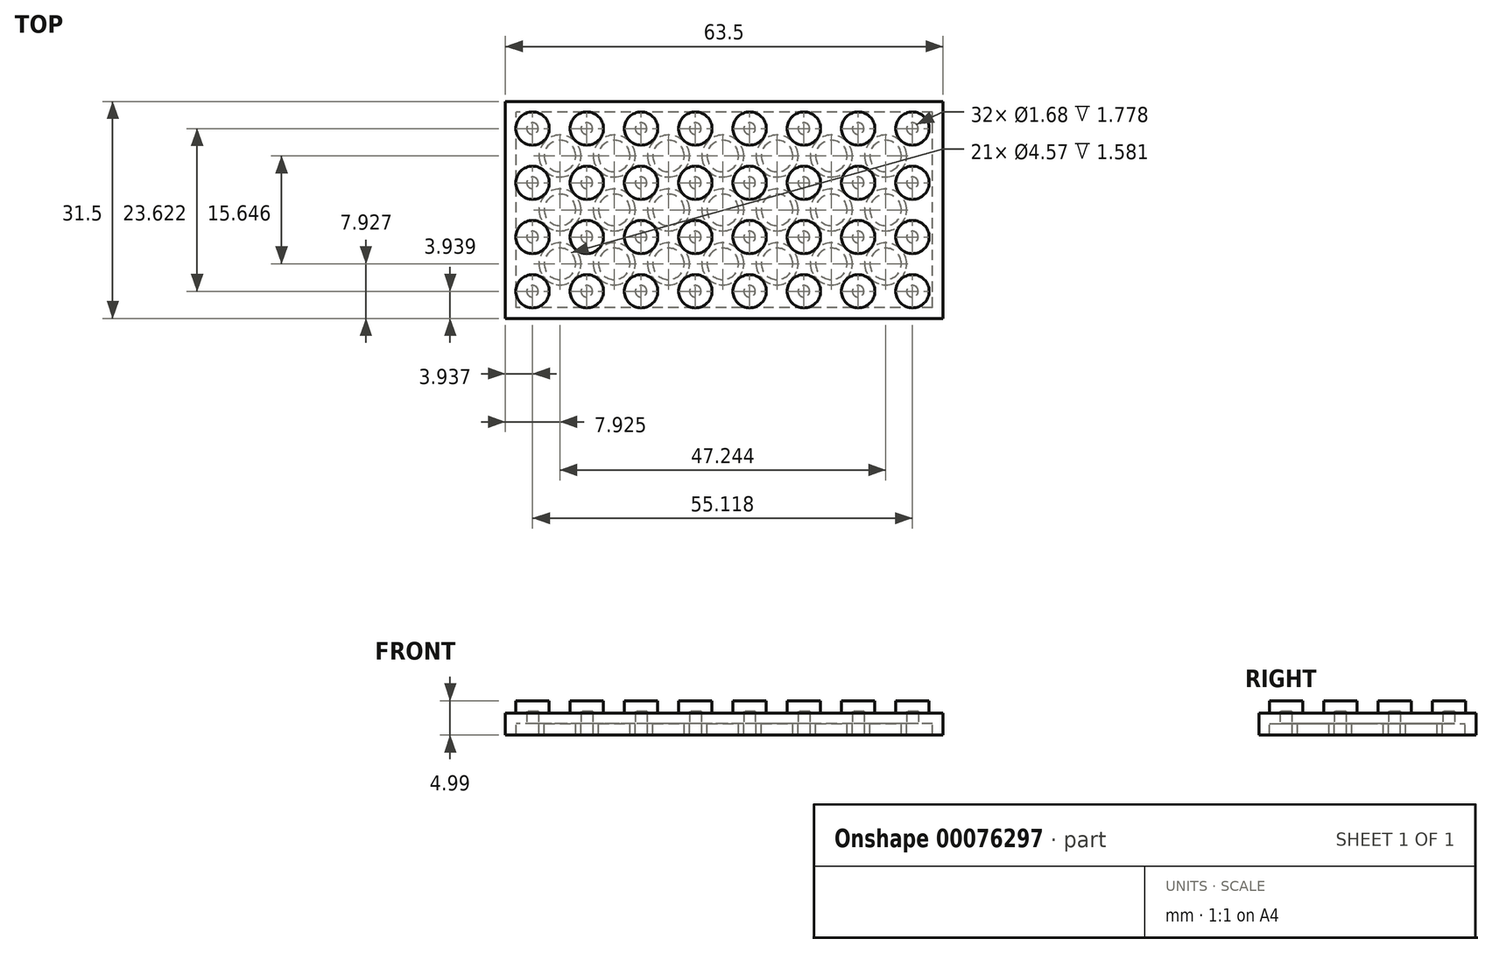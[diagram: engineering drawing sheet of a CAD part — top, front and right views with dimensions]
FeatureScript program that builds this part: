
annotation { "Feature Type Name" : "Feature", "Feature Type Description" : "" }
export const myFeature = defineFeature(function(context is Context, id is Id, definition is map)
    precondition{}
    {
        {
            var Q0;
            Q0=qCreatedBy(makeId("Top.planeOp"),FACE);
            var sketch = newSketch(context, id + "F0", { "sketchPlane" : qUnion([Q0])});
            skLineSegment(sketch, "E0.bottom", {"start": v(31.75, -15.75) * mm, "end": v(-31.75, -15.75) * mm});
            skLineSegment(sketch, "E0.top", {"start": v(31.75, 15.75) * mm, "end": v(-31.75, 15.75) * mm});
            skLineSegment(sketch, "E0.left", {"start": v(31.75, -15.75) * mm, "end": v(31.75, 15.75) * mm});
            skLineSegment(sketch, "E0.right", {"start": v(-31.75, -15.75) * mm, "end": v(-31.75, 15.75) * mm});
            skPoint(sketch, "E0.middle", {"position": v(0, 0) * mm});
            skSolve(sketch);
        }
        {
            var Q0;
            Q0=makeQuery(id+"F0.imprint","IMPRINT",FACE,{"disambiguationData":[TD([[makeQuery(id+"F0.imprint","IMPRINT",EDGE,{"derivedFrom":sQuery(id+"F0.wireOp",EDGE,"E0.bottom")}),-1.0]])]});
            extrude(context, id + "F1", {"entities" : qUnion([Q0]), "oppositeDirection" : true, "depth" : 3.2 * mm});
        }
        {
            var Q0;
            Q0=makeQuery(id+"F1.opExtrude","CAP_FACE",FACE,{"disambiguationData":[OSD([sQuery(id+"F0.wireOp",EDGE,"E0.bottom"),sQuery(id+"F0.wireOp",EDGE,"E0.top"),sQuery(id+"F0.wireOp",EDGE,"E0.left"),sQuery(id+"F0.wireOp",EDGE,"E0.right")])],"isStart":true});
            var sketch = newSketch(context, id + "F2", { "sketchPlane" : qUnion([Q0])});
            skCircle(sketch, "E1", {"center": v(-27.81, 11.81) * mm, "radius": 2.41 * mm});
            skCircle(sketch, "E2", {"center": v(-27.81, 3.94) * mm, "radius": 2.41 * mm});
            skCircle(sketch, "E3", {"center": v(-27.81, -3.94) * mm, "radius": 2.41 * mm});
            skCircle(sketch, "E4", {"center": v(-27.81, -11.81) * mm, "radius": 2.41 * mm});
            skCircle(sketch, "E5.1.0.0", {"center": v(-19.94, 11.81) * mm, "radius": 2.41 * mm});
            skCircle(sketch, "E5.1.0.1", {"center": v(-19.94, 3.94) * mm, "radius": 2.41 * mm});
            skCircle(sketch, "E5.1.0.2", {"center": v(-19.94, -3.94) * mm, "radius": 2.41 * mm});
            skCircle(sketch, "E5.1.0.3", {"center": v(-19.94, -11.81) * mm, "radius": 2.41 * mm});
            skCircle(sketch, "E5.2.0.0", {"center": v(-12.07, 11.81) * mm, "radius": 2.41 * mm});
            skCircle(sketch, "E5.2.0.1", {"center": v(-12.07, 3.94) * mm, "radius": 2.41 * mm});
            skCircle(sketch, "E5.2.0.2", {"center": v(-12.07, -3.94) * mm, "radius": 2.41 * mm});
            skCircle(sketch, "E5.2.0.3", {"center": v(-12.07, -11.81) * mm, "radius": 2.41 * mm});
            skCircle(sketch, "E5.3.0.0", {"center": v(-4.2, 11.81) * mm, "radius": 2.41 * mm});
            skCircle(sketch, "E5.3.0.1", {"center": v(-4.2, 3.94) * mm, "radius": 2.41 * mm});
            skCircle(sketch, "E5.3.0.2", {"center": v(-4.2, -3.94) * mm, "radius": 2.41 * mm});
            skCircle(sketch, "E5.3.0.3", {"center": v(-4.2, -11.81) * mm, "radius": 2.41 * mm});
            skCircle(sketch, "E5.4.0.0", {"center": v(3.68, 11.81) * mm, "radius": 2.41 * mm});
            skCircle(sketch, "E5.4.0.1", {"center": v(3.68, 3.94) * mm, "radius": 2.41 * mm});
            skCircle(sketch, "E5.4.0.2", {"center": v(3.68, -3.94) * mm, "radius": 2.41 * mm});
            skCircle(sketch, "E5.4.0.3", {"center": v(3.68, -11.81) * mm, "radius": 2.41 * mm});
            skCircle(sketch, "E5.5.0.0", {"center": v(11.56, 11.81) * mm, "radius": 2.41 * mm});
            skCircle(sketch, "E5.5.0.1", {"center": v(11.56, 3.94) * mm, "radius": 2.41 * mm});
            skCircle(sketch, "E5.5.0.2", {"center": v(11.56, -3.94) * mm, "radius": 2.41 * mm});
            skCircle(sketch, "E5.5.0.3", {"center": v(11.56, -11.81) * mm, "radius": 2.41 * mm});
            skCircle(sketch, "E5.6.0.0", {"center": v(19.43, 11.81) * mm, "radius": 2.41 * mm});
            skCircle(sketch, "E5.6.0.1", {"center": v(19.43, 3.94) * mm, "radius": 2.41 * mm});
            skCircle(sketch, "E5.6.0.2", {"center": v(19.43, -3.94) * mm, "radius": 2.41 * mm});
            skCircle(sketch, "E5.6.0.3", {"center": v(19.43, -11.81) * mm, "radius": 2.41 * mm});
            skCircle(sketch, "E5.7.0.0", {"center": v(27.3, 11.81) * mm, "radius": 2.41 * mm});
            skCircle(sketch, "E5.7.0.1", {"center": v(27.3, 3.94) * mm, "radius": 2.41 * mm});
            skCircle(sketch, "E5.7.0.2", {"center": v(27.3, -3.94) * mm, "radius": 2.41 * mm});
            skCircle(sketch, "E5.7.0.3", {"center": v(27.3, -11.81) * mm, "radius": 2.41 * mm});
            skLineSegment(sketch, "E5.direction1", {"start": v(-27.81, 11.81) * mm, "end": v(-19.94, 11.81) * mm, "construction": true});
            skSolve(sketch);
        }
        {
            var Q0;
            Q0=makeQuery(id+"F2.imprint","IMPRINT",FACE,{"disambiguationData":[TD([[makeQuery(id+"F2.imprint","IMPRINT",EDGE,{"derivedFrom":sQuery(id+"F2.wireOp",EDGE,"E1")}),1.0]])]});
            var Q1;
            Q1=makeQuery(id+"F2.imprint","IMPRINT",FACE,{"disambiguationData":[TD([[makeQuery(id+"F2.imprint","IMPRINT",EDGE,{"derivedFrom":sQuery(id+"F2.wireOp",EDGE,"E5.1.0.0")}),1.0]])]});
            var Q2;
            Q2=makeQuery(id+"F2.imprint","IMPRINT",FACE,{"disambiguationData":[TD([[makeQuery(id+"F2.imprint","IMPRINT",EDGE,{"derivedFrom":sQuery(id+"F2.wireOp",EDGE,"E5.2.0.0")}),1.0]])]});
            var Q3;
            Q3=makeQuery(id+"F2.imprint","IMPRINT",FACE,{"disambiguationData":[TD([[makeQuery(id+"F2.imprint","IMPRINT",EDGE,{"derivedFrom":sQuery(id+"F2.wireOp",EDGE,"E5.3.0.0")}),1.0]])]});
            var Q4;
            Q4=makeQuery(id+"F2.imprint","IMPRINT",FACE,{"disambiguationData":[TD([[makeQuery(id+"F2.imprint","IMPRINT",EDGE,{"derivedFrom":sQuery(id+"F2.wireOp",EDGE,"E5.4.0.0")}),1.0]])]});
            var Q5;
            Q5=makeQuery(id+"F2.imprint","IMPRINT",FACE,{"disambiguationData":[TD([[makeQuery(id+"F2.imprint","IMPRINT",EDGE,{"derivedFrom":sQuery(id+"F2.wireOp",EDGE,"E5.5.0.0")}),1.0]])]});
            var Q6;
            Q6=makeQuery(id+"F2.imprint","IMPRINT",FACE,{"disambiguationData":[TD([[makeQuery(id+"F2.imprint","IMPRINT",EDGE,{"derivedFrom":sQuery(id+"F2.wireOp",EDGE,"E5.6.0.0")}),1.0]])]});
            var Q7;
            Q7=makeQuery(id+"F2.imprint","IMPRINT",FACE,{"disambiguationData":[TD([[makeQuery(id+"F2.imprint","IMPRINT",EDGE,{"derivedFrom":sQuery(id+"F2.wireOp",EDGE,"E5.7.0.0")}),1.0]])]});
            var Q8;
            Q8=makeQuery(id+"F2.imprint","IMPRINT",FACE,{"disambiguationData":[TD([[makeQuery(id+"F2.imprint","IMPRINT",EDGE,{"derivedFrom":sQuery(id+"F2.wireOp",EDGE,"E5.7.0.1")}),1.0]])]});
            var Q9;
            Q9=makeQuery(id+"F2.imprint","IMPRINT",FACE,{"disambiguationData":[TD([[makeQuery(id+"F2.imprint","IMPRINT",EDGE,{"derivedFrom":sQuery(id+"F2.wireOp",EDGE,"E5.6.0.1")}),1.0]])]});
            var Q10;
            Q10=makeQuery(id+"F2.imprint","IMPRINT",FACE,{"disambiguationData":[TD([[makeQuery(id+"F2.imprint","IMPRINT",EDGE,{"derivedFrom":sQuery(id+"F2.wireOp",EDGE,"E5.5.0.1")}),1.0]])]});
            var Q11;
            Q11=makeQuery(id+"F2.imprint","IMPRINT",FACE,{"disambiguationData":[TD([[makeQuery(id+"F2.imprint","IMPRINT",EDGE,{"derivedFrom":sQuery(id+"F2.wireOp",EDGE,"E5.4.0.1")}),1.0]])]});
            var Q12;
            Q12=makeQuery(id+"F2.imprint","IMPRINT",FACE,{"disambiguationData":[TD([[makeQuery(id+"F2.imprint","IMPRINT",EDGE,{"derivedFrom":sQuery(id+"F2.wireOp",EDGE,"E5.3.0.1")}),1.0]])]});
            var Q13;
            Q13=makeQuery(id+"F2.imprint","IMPRINT",FACE,{"disambiguationData":[TD([[makeQuery(id+"F2.imprint","IMPRINT",EDGE,{"derivedFrom":sQuery(id+"F2.wireOp",EDGE,"E5.2.0.1")}),1.0]])]});
            var Q14;
            Q14=makeQuery(id+"F2.imprint","IMPRINT",FACE,{"disambiguationData":[TD([[makeQuery(id+"F2.imprint","IMPRINT",EDGE,{"derivedFrom":sQuery(id+"F2.wireOp",EDGE,"E5.1.0.1")}),1.0]])]});
            var Q15;
            Q15=makeQuery(id+"F2.imprint","IMPRINT",FACE,{"disambiguationData":[TD([[makeQuery(id+"F2.imprint","IMPRINT",EDGE,{"derivedFrom":sQuery(id+"F2.wireOp",EDGE,"E2")}),1.0]])]});
            var Q16;
            Q16=makeQuery(id+"F2.imprint","IMPRINT",FACE,{"disambiguationData":[TD([[makeQuery(id+"F2.imprint","IMPRINT",EDGE,{"derivedFrom":sQuery(id+"F2.wireOp",EDGE,"E3")}),1.0]])]});
            var Q17;
            Q17=makeQuery(id+"F2.imprint","IMPRINT",FACE,{"disambiguationData":[TD([[makeQuery(id+"F2.imprint","IMPRINT",EDGE,{"derivedFrom":sQuery(id+"F2.wireOp",EDGE,"E5.1.0.2")}),1.0]])]});
            var Q18;
            Q18=makeQuery(id+"F2.imprint","IMPRINT",FACE,{"disambiguationData":[TD([[makeQuery(id+"F2.imprint","IMPRINT",EDGE,{"derivedFrom":sQuery(id+"F2.wireOp",EDGE,"E5.2.0.2")}),1.0]])]});
            var Q19;
            Q19=makeQuery(id+"F2.imprint","IMPRINT",FACE,{"disambiguationData":[TD([[makeQuery(id+"F2.imprint","IMPRINT",EDGE,{"derivedFrom":sQuery(id+"F2.wireOp",EDGE,"E5.3.0.2")}),1.0]])]});
            var Q20;
            Q20=makeQuery(id+"F2.imprint","IMPRINT",FACE,{"disambiguationData":[TD([[makeQuery(id+"F2.imprint","IMPRINT",EDGE,{"derivedFrom":sQuery(id+"F2.wireOp",EDGE,"E5.4.0.2")}),1.0]])]});
            var Q21;
            Q21=makeQuery(id+"F2.imprint","IMPRINT",FACE,{"disambiguationData":[TD([[makeQuery(id+"F2.imprint","IMPRINT",EDGE,{"derivedFrom":sQuery(id+"F2.wireOp",EDGE,"E5.5.0.2")}),1.0]])]});
            var Q22;
            Q22=makeQuery(id+"F2.imprint","IMPRINT",FACE,{"disambiguationData":[TD([[makeQuery(id+"F2.imprint","IMPRINT",EDGE,{"derivedFrom":sQuery(id+"F2.wireOp",EDGE,"E5.6.0.2")}),1.0]])]});
            var Q23;
            Q23=makeQuery(id+"F2.imprint","IMPRINT",FACE,{"disambiguationData":[TD([[makeQuery(id+"F2.imprint","IMPRINT",EDGE,{"derivedFrom":sQuery(id+"F2.wireOp",EDGE,"E5.7.0.2")}),1.0]])]});
            var Q24;
            Q24=makeQuery(id+"F2.imprint","IMPRINT",FACE,{"disambiguationData":[TD([[makeQuery(id+"F2.imprint","IMPRINT",EDGE,{"derivedFrom":sQuery(id+"F2.wireOp",EDGE,"E5.7.0.3")}),1.0]])]});
            var Q25;
            Q25=makeQuery(id+"F2.imprint","IMPRINT",FACE,{"disambiguationData":[TD([[makeQuery(id+"F2.imprint","IMPRINT",EDGE,{"derivedFrom":sQuery(id+"F2.wireOp",EDGE,"E5.6.0.3")}),1.0]])]});
            var Q26;
            Q26=makeQuery(id+"F2.imprint","IMPRINT",FACE,{"disambiguationData":[TD([[makeQuery(id+"F2.imprint","IMPRINT",EDGE,{"derivedFrom":sQuery(id+"F2.wireOp",EDGE,"E5.5.0.3")}),1.0]])]});
            var Q27;
            Q27=makeQuery(id+"F2.imprint","IMPRINT",FACE,{"disambiguationData":[TD([[makeQuery(id+"F2.imprint","IMPRINT",EDGE,{"derivedFrom":sQuery(id+"F2.wireOp",EDGE,"E5.3.0.3")}),1.0]])]});
            var Q28;
            Q28=makeQuery(id+"F2.imprint","IMPRINT",FACE,{"disambiguationData":[TD([[makeQuery(id+"F2.imprint","IMPRINT",EDGE,{"derivedFrom":sQuery(id+"F2.wireOp",EDGE,"E5.2.0.3")}),1.0]])]});
            var Q29;
            Q29=makeQuery(id+"F2.imprint","IMPRINT",FACE,{"disambiguationData":[TD([[makeQuery(id+"F2.imprint","IMPRINT",EDGE,{"derivedFrom":sQuery(id+"F2.wireOp",EDGE,"E5.1.0.3")}),1.0]])]});
            var Q30;
            Q30=makeQuery(id+"F2.imprint","IMPRINT",FACE,{"disambiguationData":[TD([[makeQuery(id+"F2.imprint","IMPRINT",EDGE,{"derivedFrom":sQuery(id+"F2.wireOp",EDGE,"E4")}),1.0]])]});
            var Q31;
            Q31=makeQuery(id+"F2.imprint","IMPRINT",FACE,{"disambiguationData":[TD([[makeQuery(id+"F2.imprint","IMPRINT",EDGE,{"derivedFrom":sQuery(id+"F2.wireOp",EDGE,"E5.4.0.3")}),1.0]])]});
            extrude(context, id + "F3", {"entities" : qUnion([Q0, Q1, Q2, Q3, Q4, Q5, Q6, Q7, Q8, Q9, Q10, Q11, Q12, Q13, Q14, Q15, Q16, Q17, Q18, Q19, Q20, Q21, Q22, Q23, Q24, Q25, Q26, Q27, Q28, Q29, Q30, Q31]), "operationType" : NewBodyOperationType.ADD, "depth" : 1.78 * mm});
        }
        {
            var Q0;
            Q0=makeQuery(id+"F1.opExtrude","CAP_FACE",FACE,{"disambiguationData":[OSD([sQuery(id+"F0.wireOp",EDGE,"E0.bottom"),sQuery(id+"F0.wireOp",EDGE,"E0.top"),sQuery(id+"F0.wireOp",EDGE,"E0.left"),sQuery(id+"F0.wireOp",EDGE,"E0.right")])],"isStart":false});
            shell(context, id + "F4", {"entities" : qUnion([Q0]), "thickness" : 1.57 * mm});
        }
        {
            var Q0;
            Q0=makeQuery(id+"F4.opShell","OFFSET_FACE",FACE,{"disambiguationData":[OSD([sQuery(id+"F0.wireOp",EDGE,"E0.bottom"),sQuery(id+"F0.wireOp",EDGE,"E0.top"),sQuery(id+"F0.wireOp",EDGE,"E0.left"),sQuery(id+"F0.wireOp",EDGE,"E0.right")])]});
            var sketch = newSketch(context, id + "F5", { "sketchPlane" : qUnion([Q0])});
            skSolve(sketch);
        }
        {
            var Q0;
            {var subQ19=sQuery(id+"F0.wireOp",EDGE,"E0.bottom");Q0=makeQuery(id+"F5.imprint","IMPRINT",FACE,{"disambiguationData":[TD([[makeQuery(id+"F5.imprint","IMPRINT",EDGE,{"derivedFrom":makeQuery(id+"F4.opShell","OFFSET_EDGE",EDGE,{"disambiguationData":[OSD([subQ19]),TDD([makeQuery(id+"F1.opExtrude","CAP_EDGE",EDGE,{"disambiguationData":[OSD([subQ19])],"isStart":true})])]})}),1.0]])]});}
            var sketch = newSketch(context, id + "F6", { "sketchPlane" : qUnion([Q0])});
            skCircle(sketch, "E6", {"center": v(-23.83, 7.82) * mm, "radius": 3.05 * mm});
            skCircle(sketch, "E7", {"center": v(-23.83, 0) * mm, "radius": 3.05 * mm});
            skCircle(sketch, "E8", {"center": v(-23.83, -7.82) * mm, "radius": 3.05 * mm});
            skCircle(sketch, "E9.1.0.0", {"center": v(-15.95, 7.82) * mm, "radius": 3.05 * mm});
            skCircle(sketch, "E9.1.0.1", {"center": v(-15.95, 0) * mm, "radius": 3.05 * mm});
            skCircle(sketch, "E9.1.0.2", {"center": v(-15.95, -7.82) * mm, "radius": 3.05 * mm});
            skCircle(sketch, "E9.2.0.0", {"center": v(-8.08, 7.82) * mm, "radius": 3.05 * mm});
            skCircle(sketch, "E9.2.0.1", {"center": v(-8.08, 0) * mm, "radius": 3.05 * mm});
            skCircle(sketch, "E9.2.0.2", {"center": v(-8.08, -7.82) * mm, "radius": 3.05 * mm});
            skCircle(sketch, "E9.3.0.0", {"center": v(-0.2, 7.82) * mm, "radius": 3.05 * mm});
            skCircle(sketch, "E9.3.0.1", {"center": v(-0.2, 0) * mm, "radius": 3.05 * mm});
            skCircle(sketch, "E9.3.0.2", {"center": v(-0.2, -7.82) * mm, "radius": 3.05 * mm});
            skCircle(sketch, "E9.4.0.0", {"center": v(7.67, 7.82) * mm, "radius": 3.05 * mm});
            skCircle(sketch, "E9.4.0.1", {"center": v(7.67, 0) * mm, "radius": 3.05 * mm});
            skCircle(sketch, "E9.4.0.2", {"center": v(7.67, -7.82) * mm, "radius": 3.05 * mm});
            skCircle(sketch, "E9.5.0.0", {"center": v(15.54, 7.82) * mm, "radius": 3.05 * mm});
            skCircle(sketch, "E9.5.0.1", {"center": v(15.54, 0) * mm, "radius": 3.05 * mm});
            skCircle(sketch, "E9.5.0.2", {"center": v(15.54, -7.82) * mm, "radius": 3.05 * mm});
            skCircle(sketch, "E9.6.0.0", {"center": v(23.42, 7.82) * mm, "radius": 3.05 * mm});
            skCircle(sketch, "E9.6.0.1", {"center": v(23.42, 0) * mm, "radius": 3.05 * mm});
            skCircle(sketch, "E9.6.0.2", {"center": v(23.42, -7.82) * mm, "radius": 3.05 * mm});
            skCircle(sketch, "E10", {"center": v(-23.83, 7.82) * mm, "radius": 2.29 * mm});
            skCircle(sketch, "E11", {"center": v(-23.83, 0) * mm, "radius": 2.29 * mm});
            skCircle(sketch, "E12", {"center": v(-23.83, -7.82) * mm, "radius": 2.29 * mm});
            skCircle(sketch, "E13.1.0.0", {"center": v(-15.95, 7.82) * mm, "radius": 2.29 * mm});
            skCircle(sketch, "E13.1.0.1", {"center": v(-15.95, 0) * mm, "radius": 2.29 * mm});
            skCircle(sketch, "E13.1.0.2", {"center": v(-15.95, -7.82) * mm, "radius": 2.29 * mm});
            skCircle(sketch, "E13.2.0.0", {"center": v(-8.08, 7.82) * mm, "radius": 2.29 * mm});
            skCircle(sketch, "E13.2.0.1", {"center": v(-8.08, 0) * mm, "radius": 2.29 * mm});
            skCircle(sketch, "E13.2.0.2", {"center": v(-8.08, -7.82) * mm, "radius": 2.29 * mm});
            skCircle(sketch, "E13.3.0.0", {"center": v(-0.2, 7.82) * mm, "radius": 2.29 * mm});
            skCircle(sketch, "E13.3.0.1", {"center": v(-0.2, 0) * mm, "radius": 2.29 * mm});
            skCircle(sketch, "E13.3.0.2", {"center": v(-0.2, -7.82) * mm, "radius": 2.29 * mm});
            skCircle(sketch, "E13.4.0.0", {"center": v(7.67, 7.82) * mm, "radius": 2.29 * mm});
            skCircle(sketch, "E13.4.0.1", {"center": v(7.67, 0) * mm, "radius": 2.29 * mm});
            skCircle(sketch, "E13.4.0.2", {"center": v(7.67, -7.82) * mm, "radius": 2.29 * mm});
            skCircle(sketch, "E13.5.0.0", {"center": v(15.54, 7.82) * mm, "radius": 2.29 * mm});
            skCircle(sketch, "E13.5.0.1", {"center": v(15.54, 0) * mm, "radius": 2.29 * mm});
            skCircle(sketch, "E13.5.0.2", {"center": v(15.54, -7.82) * mm, "radius": 2.29 * mm});
            skCircle(sketch, "E13.6.0.0", {"center": v(23.42, 7.82) * mm, "radius": 2.29 * mm});
            skCircle(sketch, "E13.6.0.1", {"center": v(23.42, 0) * mm, "radius": 2.29 * mm});
            skCircle(sketch, "E13.6.0.2", {"center": v(23.42, -7.82) * mm, "radius": 2.29 * mm});
            skSolve(sketch);
        }
        {
            var Q0;
            Q0=makeQuery(id+"F6.imprint","IMPRINT",FACE,{"disambiguationData":[TD([[makeQuery(id+"F6.imprint","IMPRINT",EDGE,{"derivedFrom":sQuery(id+"F6.wireOp",EDGE,"E9.3.0.1")}),1.0]])]});
            var Q1;
            Q1=makeQuery(id+"F6.imprint","IMPRINT",FACE,{"disambiguationData":[TD([[makeQuery(id+"F6.imprint","IMPRINT",EDGE,{"derivedFrom":sQuery(id+"F6.wireOp",EDGE,"E9.6.0.1")}),1.0]])]});
            var Q2;
            Q2=makeQuery(id+"F6.imprint","IMPRINT",FACE,{"disambiguationData":[TD([[makeQuery(id+"F6.imprint","IMPRINT",EDGE,{"derivedFrom":sQuery(id+"F6.wireOp",EDGE,"E9.6.0.2")}),1.0]])]});
            var Q3;
            Q3=makeQuery(id+"F6.imprint","IMPRINT",FACE,{"disambiguationData":[TD([[makeQuery(id+"F6.imprint","IMPRINT",EDGE,{"derivedFrom":sQuery(id+"F6.wireOp",EDGE,"E9.5.0.2")}),1.0]])]});
            var Q4;
            Q4=makeQuery(id+"F6.imprint","IMPRINT",FACE,{"disambiguationData":[TD([[makeQuery(id+"F6.imprint","IMPRINT",EDGE,{"derivedFrom":sQuery(id+"F6.wireOp",EDGE,"E9.6.0.0")}),1.0]])]});
            var Q5;
            Q5=makeQuery(id+"F6.imprint","IMPRINT",FACE,{"disambiguationData":[TD([[makeQuery(id+"F6.imprint","IMPRINT",EDGE,{"derivedFrom":sQuery(id+"F6.wireOp",EDGE,"E9.5.0.1")}),1.0]])]});
            var Q6;
            Q6=makeQuery(id+"F6.imprint","IMPRINT",FACE,{"disambiguationData":[TD([[makeQuery(id+"F6.imprint","IMPRINT",EDGE,{"derivedFrom":sQuery(id+"F6.wireOp",EDGE,"E9.5.0.0")}),1.0]])]});
            var Q7;
            Q7=makeQuery(id+"F6.imprint","IMPRINT",FACE,{"disambiguationData":[TD([[makeQuery(id+"F6.imprint","IMPRINT",EDGE,{"derivedFrom":sQuery(id+"F6.wireOp",EDGE,"E9.4.0.1")}),1.0]])]});
            var Q8;
            Q8=makeQuery(id+"F6.imprint","IMPRINT",FACE,{"disambiguationData":[TD([[makeQuery(id+"F6.imprint","IMPRINT",EDGE,{"derivedFrom":sQuery(id+"F6.wireOp",EDGE,"E9.3.0.2")}),1.0]])]});
            var Q9;
            Q9=makeQuery(id+"F6.imprint","IMPRINT",FACE,{"disambiguationData":[TD([[makeQuery(id+"F6.imprint","IMPRINT",EDGE,{"derivedFrom":sQuery(id+"F6.wireOp",EDGE,"E9.4.0.0")}),1.0]])]});
            var Q10;
            Q10=makeQuery(id+"F6.imprint","IMPRINT",FACE,{"disambiguationData":[TD([[makeQuery(id+"F6.imprint","IMPRINT",EDGE,{"derivedFrom":sQuery(id+"F6.wireOp",EDGE,"E9.3.0.0")}),1.0]])]});
            var Q11;
            Q11=makeQuery(id+"F6.imprint","IMPRINT",FACE,{"disambiguationData":[TD([[makeQuery(id+"F6.imprint","IMPRINT",EDGE,{"derivedFrom":sQuery(id+"F6.wireOp",EDGE,"E9.2.0.2")}),1.0]])]});
            var Q12;
            Q12=makeQuery(id+"F6.imprint","IMPRINT",FACE,{"disambiguationData":[TD([[makeQuery(id+"F6.imprint","IMPRINT",EDGE,{"derivedFrom":sQuery(id+"F6.wireOp",EDGE,"E9.4.0.2")}),1.0]])]});
            var Q13;
            Q13=makeQuery(id+"F6.imprint","IMPRINT",FACE,{"disambiguationData":[TD([[makeQuery(id+"F6.imprint","IMPRINT",EDGE,{"derivedFrom":sQuery(id+"F6.wireOp",EDGE,"E7")}),1.0]])]});
            var Q14;
            Q14=makeQuery(id+"F6.imprint","IMPRINT",FACE,{"disambiguationData":[TD([[makeQuery(id+"F6.imprint","IMPRINT",EDGE,{"derivedFrom":sQuery(id+"F6.wireOp",EDGE,"E6")}),1.0]])]});
            var Q15;
            Q15=makeQuery(id+"F6.imprint","IMPRINT",FACE,{"disambiguationData":[TD([[makeQuery(id+"F6.imprint","IMPRINT",EDGE,{"derivedFrom":sQuery(id+"F6.wireOp",EDGE,"E9.2.0.0")}),1.0]])]});
            var Q16;
            Q16=makeQuery(id+"F6.imprint","IMPRINT",FACE,{"disambiguationData":[TD([[makeQuery(id+"F6.imprint","IMPRINT",EDGE,{"derivedFrom":sQuery(id+"F6.wireOp",EDGE,"E9.1.0.0")}),1.0]])]});
            var Q17;
            Q17=makeQuery(id+"F6.imprint","IMPRINT",FACE,{"disambiguationData":[TD([[makeQuery(id+"F6.imprint","IMPRINT",EDGE,{"derivedFrom":sQuery(id+"F6.wireOp",EDGE,"E9.2.0.1")}),1.0]])]});
            var Q18;
            Q18=makeQuery(id+"F6.imprint","IMPRINT",FACE,{"disambiguationData":[TD([[makeQuery(id+"F6.imprint","IMPRINT",EDGE,{"derivedFrom":sQuery(id+"F6.wireOp",EDGE,"E9.1.0.1")}),1.0]])]});
            var Q19;
            Q19=makeQuery(id+"F6.imprint","IMPRINT",FACE,{"disambiguationData":[TD([[makeQuery(id+"F6.imprint","IMPRINT",EDGE,{"derivedFrom":sQuery(id+"F6.wireOp",EDGE,"E9.1.0.2")}),1.0]])]});
            var Q20;
            Q20=makeQuery(id+"F6.imprint","IMPRINT",FACE,{"disambiguationData":[TD([[makeQuery(id+"F6.imprint","IMPRINT",EDGE,{"derivedFrom":sQuery(id+"F6.wireOp",EDGE,"E8")}),1.0]])]});
            extrude(context, id + "F7", {"entities" : qUnion([Q0, Q1, Q2, Q3, Q4, Q5, Q6, Q7, Q8, Q9, Q10, Q11, Q12, Q13, Q14, Q15, Q16, Q17, Q18, Q19, Q20]), "operationType" : NewBodyOperationType.ADD, "depth" : 1.58 * mm});
        }
    });
